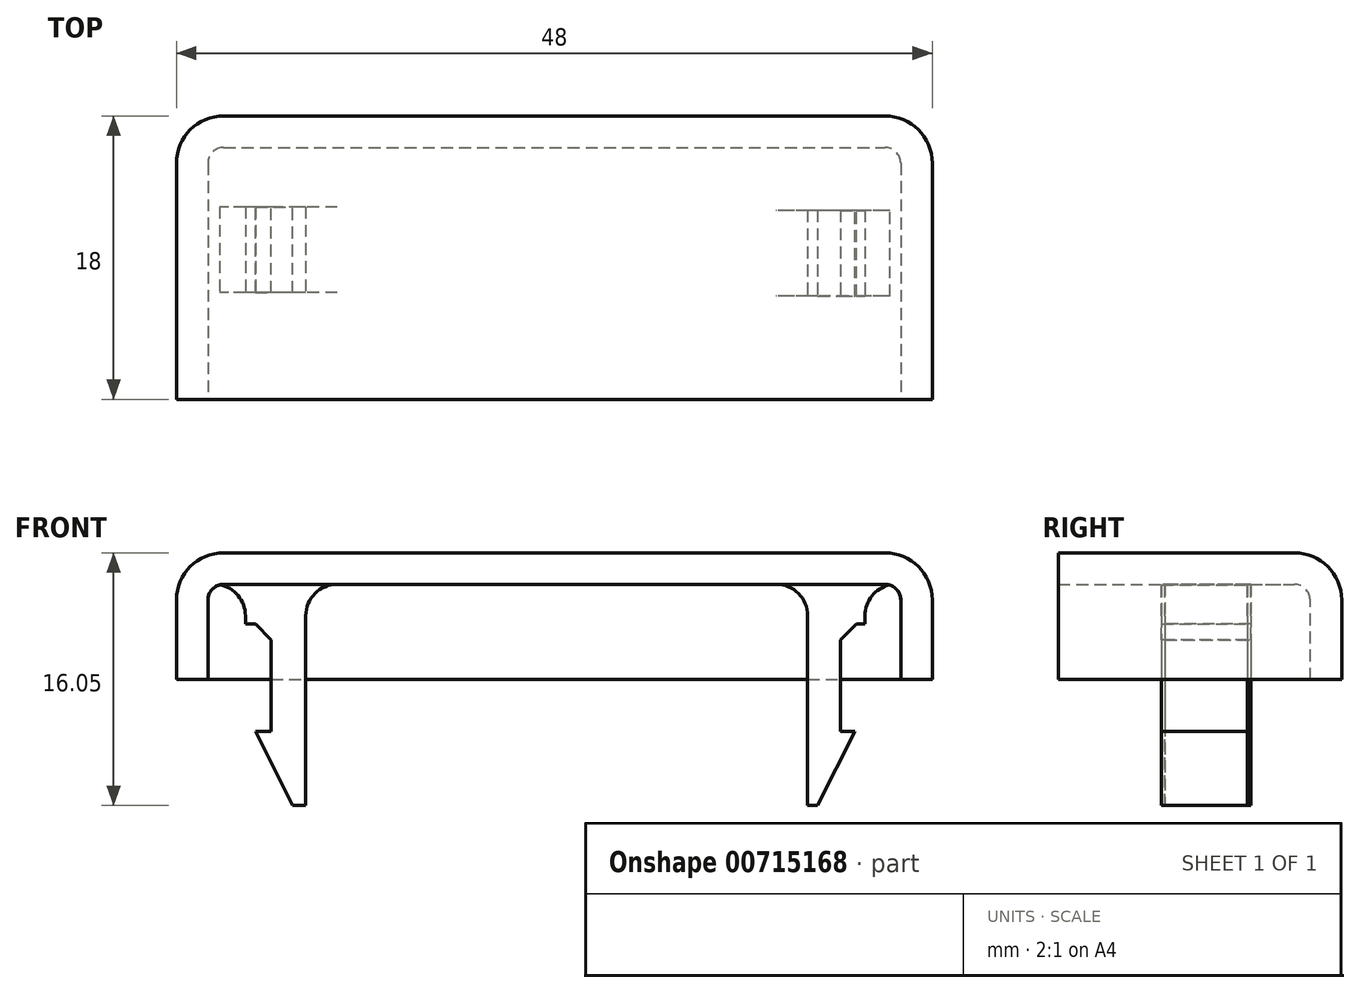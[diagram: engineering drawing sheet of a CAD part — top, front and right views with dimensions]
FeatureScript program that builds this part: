
annotation { "Feature Type Name" : "Feature", "Feature Type Description" : "" }
export const myFeature = defineFeature(function(context is Context, id is Id, definition is map)
    precondition{}
    {
        {
            var Q0;
            Q0=qCreatedBy(makeId("Front.planeOp"),FACE);
            var sketch = newSketch(context, id + "F0", { "sketchPlane" : qUnion([Q0])});
            skLineSegment(sketch, "E0.bottom", {"start": v(-16.63, 0) * mm, "end": v(31.37, 0) * mm});
            skLineSegment(sketch, "E0.top", {"start": v(-16.63, 8.05) * mm, "end": v(31.37, 8.05) * mm});
            skLineSegment(sketch, "E0.left", {"start": v(-16.63, 0) * mm, "end": v(-16.63, 8.05) * mm});
            skLineSegment(sketch, "E0.right", {"start": v(31.37, 0) * mm, "end": v(31.37, 8.05) * mm});
            skSolve(sketch);
        }
        {
            var Q0;
            Q0=makeQuery(id+"F0.imprint","IMPRINT",FACE,{"disambiguationData":[TD([[makeQuery(id+"F0.imprint","IMPRINT",EDGE,{"derivedFrom":sQuery(id+"F0.wireOp",EDGE,"E0.bottom")}),1.0]])]});
            extrude(context, id + "F1", {"entities" : qUnion([Q0]), "oppositeDirection" : true, "depth" : 18 * mm, "offsetDistance" : 25 * mm});
        }
        {
            var Q0;
            Q0=makeQuery(id+"F1.opExtrude","CAP_EDGE",EDGE,{"disambiguationData":[OSD([sQuery(id+"F0.wireOp",EDGE,"E0.top")])],"isStart":false});
            var Q1;
            Q1=makeQuery(id+"F1.opExtrude","SWEPT_EDGE",EDGE,{"disambiguationData":[OSD([sQuery(id+"F0.wireOp",EDGE,"E0.top"),sQuery(id+"F0.wireOp",EDGE,"E0.left")])]});
            var Q2;
            Q2=makeQuery(id+"F1.opExtrude","SWEPT_EDGE",EDGE,{"disambiguationData":[OSD([sQuery(id+"F0.wireOp",EDGE,"E0.top"),sQuery(id+"F0.wireOp",EDGE,"E0.right")])]});
            var Q3;
            Q3=makeQuery(id+"F1.opExtrude","CAP_EDGE",EDGE,{"disambiguationData":[OSD([sQuery(id+"F0.wireOp",EDGE,"E0.left")])],"isStart":false});
            var Q4;
            Q4=makeQuery(id+"F1.opExtrude","CAP_EDGE",EDGE,{"disambiguationData":[OSD([sQuery(id+"F0.wireOp",EDGE,"E0.right")])],"isStart":false});
            fillet(context, id + "F2", {"entities" : qUnion([Q0, Q1, Q2, Q3, Q4]), "radius" : 3 * mm, "tangentPropagation" : true, "allowEdgeOverflow" : false});
        }
        {
            var Q0;
            Q0=makeQuery(id+"F1.opExtrude","CAP_FACE",FACE,{"disambiguationData":[OSD([sQuery(id+"F0.wireOp",EDGE,"E0.bottom"),sQuery(id+"F0.wireOp",EDGE,"E0.top"),sQuery(id+"F0.wireOp",EDGE,"E0.left"),sQuery(id+"F0.wireOp",EDGE,"E0.right")])],"isStart":true});
            var Q1;
            Q1=makeQuery(id+"F1.opExtrude","SWEPT_FACE",FACE,{"disambiguationData":[OSD([sQuery(id+"F0.wireOp",EDGE,"E0.bottom")])]});
            shell(context, id + "F3", {"entities" : qUnion([Q0, Q1]), "thickness" : 2 * mm});
        }
        {
            var Q0;
            Q0=qCreatedBy(makeId("Top.planeOp"),FACE);
            var sketch = newSketch(context, id + "F4", { "sketchPlane" : qUnion([Q0])});
            skLineSegment(sketch, "E1.bottom", {"start": v(27.1, 12) * mm, "end": v(23.45, 12) * mm});
            skLineSegment(sketch, "E1.top", {"start": v(27.1, 6.55) * mm, "end": v(23.45, 6.55) * mm});
            skLineSegment(sketch, "E1.left", {"start": v(27.1, 12) * mm, "end": v(27.1, 6.55) * mm});
            skLineSegment(sketch, "E1.right", {"start": v(23.45, 12) * mm, "end": v(23.45, 6.55) * mm});
            skSolve(sketch);
        }
        {
            var Q0;
            Q0=makeQuery(id+"F4.imprint","IMPRINT",FACE,{"disambiguationData":[TD([[makeQuery(id+"F4.imprint","IMPRINT",EDGE,{"derivedFrom":sQuery(id+"F4.wireOp",EDGE,"E1.bottom")}),1.0]])]});
            extrude(context, id + "F5", {"entities" : qUnion([Q0]), "operationType" : NewBodyOperationType.ADD, "endBound" : BoundingType.SYMMETRIC, "depth" : 16 * mm, "offsetDistance" : 25 * mm});
        }
        {
            var Q0;
            Q0=qCreatedBy(makeId("Top.planeOp"),FACE);
            var sketch = newSketch(context, id + "F6", { "sketchPlane" : qUnion([Q0])});
            skLineSegment(sketch, "E2.bottom", {"start": v(-8.43, 12.23) * mm, "end": v(-12.26, 12.23) * mm});
            skLineSegment(sketch, "E2.top", {"start": v(-8.43, 6.77) * mm, "end": v(-12.26, 6.77) * mm});
            skLineSegment(sketch, "E2.left", {"start": v(-8.43, 12.23) * mm, "end": v(-8.43, 6.77) * mm});
            skLineSegment(sketch, "E2.right", {"start": v(-12.26, 12.23) * mm, "end": v(-12.26, 6.77) * mm});
            skSolve(sketch);
        }
        {
            var Q0;
            Q0=makeQuery(id+"F6.imprint","IMPRINT",FACE,{"disambiguationData":[TD([[makeQuery(id+"F6.imprint","IMPRINT",EDGE,{"derivedFrom":sQuery(id+"F6.wireOp",EDGE,"E2.top")}),-1.0]])]});
            extrude(context, id + "F7", {"entities" : qUnion([Q0]), "operationType" : NewBodyOperationType.ADD, "endBound" : BoundingType.SYMMETRIC, "depth" : 16 * mm, "offsetDistance" : 25 * mm});
        }
        {
            var Q0;
            Q0=qCreatedBy(makeId("Front.planeOp"),FACE);
            var sketch = newSketch(context, id + "F8", { "sketchPlane" : qUnion([Q0])});
            skLineSegment(sketch, "E3.bottom", {"start": v(25.55, 3.52) * mm, "end": v(27.85, 3.52) * mm});
            skLineSegment(sketch, "E3.top", {"start": v(25.55, -3.3) * mm, "end": v(27.85, -3.3) * mm});
            skLineSegment(sketch, "E3.left", {"start": v(25.55, 3.52) * mm, "end": v(25.55, -3.3) * mm});
            skLineSegment(sketch, "E3.right", {"start": v(27.85, 3.52) * mm, "end": v(27.85, -3.3) * mm});
            skLineSegment(sketch, "E4.bottom", {"start": v(-10.62, 3.52) * mm, "end": v(-13.56, 3.52) * mm});
            skLineSegment(sketch, "E4.top", {"start": v(-10.62, -3.3) * mm, "end": v(-13.56, -3.3) * mm});
            skLineSegment(sketch, "E4.left", {"start": v(-10.62, 3.52) * mm, "end": v(-10.62, -3.3) * mm});
            skLineSegment(sketch, "E4.right", {"start": v(-13.56, 3.52) * mm, "end": v(-13.56, -3.3) * mm});
            skSolve(sketch);
        }
        {
            var Q0;
            Q0=makeQuery(id+"F8.imprint","IMPRINT",FACE,{"disambiguationData":[TD([[makeQuery(id+"F8.imprint","IMPRINT",EDGE,{"derivedFrom":sQuery(id+"F8.wireOp",EDGE,"E3.bottom")}),-1.0]])]});
            var Q1;
            Q1=makeQuery(id+"F8.imprint","IMPRINT",FACE,{"disambiguationData":[TD([[makeQuery(id+"F8.imprint","IMPRINT",EDGE,{"derivedFrom":sQuery(id+"F8.wireOp",EDGE,"E4.bottom")}),1.0]])]});
            extrude(context, id + "F9", {"entities" : qUnion([Q0, Q1]), "oppositeDirection" : true, "depth" : 13.4 * mm, "offsetDistance" : 25 * mm});
        }
        {
            var Q0;
            Q0=makeQuery(id+"F9.opExtrude","SWEPT_BODY",BODY,{"disambiguationData":[OSD([sQuery(id+"F8.wireOp",EDGE,"E3.bottom"),sQuery(id+"F8.wireOp",EDGE,"E3.top"),sQuery(id+"F8.wireOp",EDGE,"E3.left"),sQuery(id+"F8.wireOp",EDGE,"E3.right")])]});
            var Q1;
            Q1=makeQuery(id+"F9.opExtrude","SWEPT_BODY",BODY,{"disambiguationData":[OSD([sQuery(id+"F8.wireOp",EDGE,"E4.bottom"),sQuery(id+"F8.wireOp",EDGE,"E4.top"),sQuery(id+"F8.wireOp",EDGE,"E4.left"),sQuery(id+"F8.wireOp",EDGE,"E4.right")])]});
            var Q2;
            Q2=makeQuery(id+"F1.opExtrude","SWEPT_BODY",BODY,{"disambiguationData":[OSD([sQuery(id+"F0.wireOp",EDGE,"E0.bottom"),sQuery(id+"F0.wireOp",EDGE,"E0.top"),sQuery(id+"F0.wireOp",EDGE,"E0.left"),sQuery(id+"F0.wireOp",EDGE,"E0.right")])]});
            booleanBodies(context, id + "F10", {"operationType" : BooleanOperationType.SUBTRACTION, "tools" : qUnion([Q0, Q1]), "targets" : qUnion([Q2])});
        }
        {
            var Q0;
            Q0=makeQuery(id+"F7.opExtrude","CAP_EDGE",EDGE,{"disambiguationData":[OSD([sQuery(id+"F6.wireOp",EDGE,"E2.right")])],"isStart":true});
            chamfer(context, id + "F11", {"entities" : qUnion([Q0]), "chamferType" : ChamferType.TWO_OFFSETS, "width1" : 6 * mm, "oppositeDirection" : false, "width2" : 3 * mm, "tangentPropagation" : true});
        }
        {
            var Q0;
            Q0=makeQuery(id+"F5.opExtrude","CAP_EDGE",EDGE,{"disambiguationData":[OSD([sQuery(id+"F4.wireOp",EDGE,"E1.left")])],"isStart":true});
            chamfer(context, id + "F12", {"entities" : qUnion([Q0]), "chamferType" : ChamferType.TWO_OFFSETS, "width1" : 3 * mm, "oppositeDirection" : false, "width2" : 6 * mm, "tangentPropagation" : true});
        }
        {
            var Q0;
            {var subQ0=sQuery(id+"F0.wireOp",EDGE,"E0.top");Q0=makeQuery(id+"F7.boolean.opBoolean","INTERSECT",EDGE,{"derivedFrom":[makeQuery(id+"F3.opShell","OFFSET_FACE",FACE,{"disambiguationData":[OSD([subQ0]),TDD([makeQuery(id+"F1.opExtrude","SWEPT_FACE",FACE,{"disambiguationData":[OSD([subQ0])]})])]}),makeQuery(id+"F7.opExtrude","SWEPT_FACE",FACE,{"disambiguationData":[OSD([sQuery(id+"F6.wireOp",EDGE,"E2.left")])]})]});}
            var Q1;
            {var subQ0=sQuery(id+"F0.wireOp",EDGE,"E0.top");Q1=makeQuery(id+"F5.boolean.opBoolean","INTERSECT",EDGE,{"derivedFrom":[makeQuery(id+"F3.opShell","OFFSET_FACE",FACE,{"disambiguationData":[OSD([subQ0]),TDD([makeQuery(id+"F1.opExtrude","SWEPT_FACE",FACE,{"disambiguationData":[OSD([subQ0])]})])]}),makeQuery(id+"F5.opExtrude","SWEPT_FACE",FACE,{"disambiguationData":[OSD([sQuery(id+"F4.wireOp",EDGE,"E1.right")])]})]});}
            var Q2;
            {var subQ0=sQuery(id+"F0.wireOp",EDGE,"E0.top");Q2=makeQuery(id+"F7.boolean.opBoolean","INTERSECT",EDGE,{"derivedFrom":[makeQuery(id+"F3.opShell","OFFSET_FACE",FACE,{"disambiguationData":[OSD([subQ0]),TDD([makeQuery(id+"F1.opExtrude","SWEPT_FACE",FACE,{"disambiguationData":[OSD([subQ0])]})])]}),makeQuery(id+"F7.opExtrude","SWEPT_FACE",FACE,{"disambiguationData":[OSD([sQuery(id+"F6.wireOp",EDGE,"E2.right")])]})]});}
            var Q3;
            {var subQ0=sQuery(id+"F0.wireOp",EDGE,"E0.top");Q3=makeQuery(id+"F5.boolean.opBoolean","INTERSECT",EDGE,{"derivedFrom":[makeQuery(id+"F3.opShell","OFFSET_FACE",FACE,{"disambiguationData":[OSD([subQ0]),TDD([makeQuery(id+"F1.opExtrude","SWEPT_FACE",FACE,{"disambiguationData":[OSD([subQ0])]})])]}),makeQuery(id+"F5.opExtrude","SWEPT_FACE",FACE,{"disambiguationData":[OSD([sQuery(id+"F4.wireOp",EDGE,"E1.left")])]})]});}
            fillet(context, id + "F13", {"entities" : qUnion([Q0, Q1, Q2, Q3]), "radius" : 2 * mm, "tangentPropagation" : true, "allowEdgeOverflow" : false});
        }
        {
            var Q0;
            Q0=makeQuery(id+"F10.opBoolean","COPY",EDGE,{"derivedFrom":makeQuery(id+"F9.opExtrude","SWEPT_EDGE",EDGE,{"disambiguationData":[OSD([sQuery(id+"F8.wireOp",EDGE,"E3.bottom"),sQuery(id+"F8.wireOp",EDGE,"E3.left")])]})});
            var Q1;
            Q1=makeQuery(id+"F10.opBoolean","COPY",EDGE,{"derivedFrom":makeQuery(id+"F9.opExtrude","SWEPT_EDGE",EDGE,{"disambiguationData":[OSD([sQuery(id+"F8.wireOp",EDGE,"E4.bottom"),sQuery(id+"F8.wireOp",EDGE,"E4.left")])]})});
            chamfer(context, id + "F14", {"entities" : qUnion([Q0, Q1]), "width" : 1 * mm, "tangentPropagation" : true});
        }
    });
